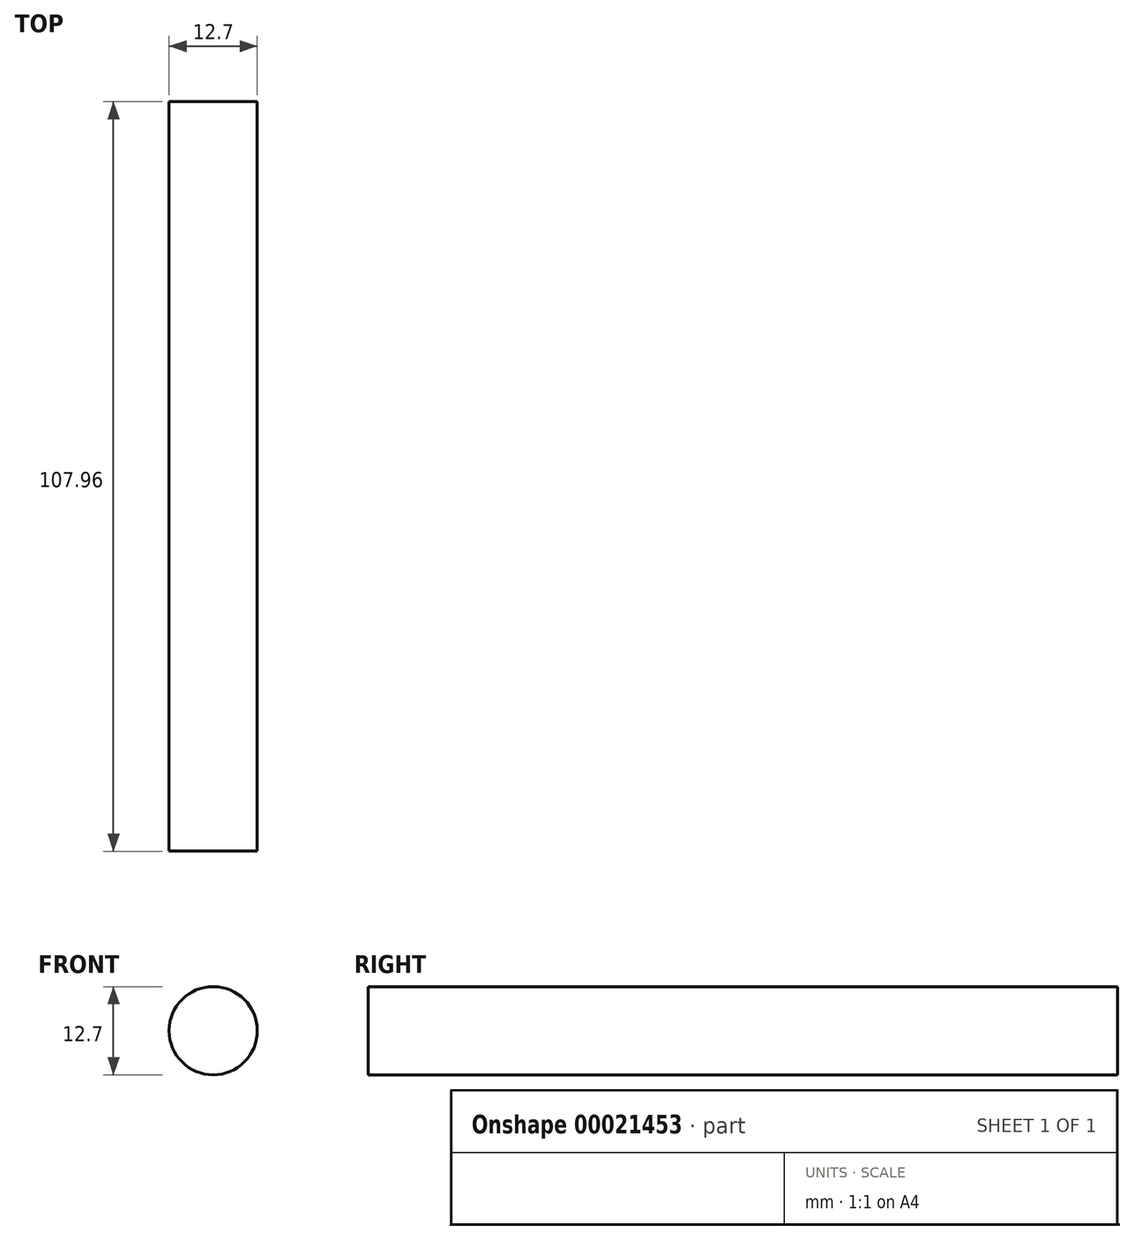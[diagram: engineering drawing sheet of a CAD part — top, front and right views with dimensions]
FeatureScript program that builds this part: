
annotation { "Feature Type Name" : "Feature", "Feature Type Description" : "" }
export const myFeature = defineFeature(function(context is Context, id is Id, definition is map)
    precondition{}
    {
        {
            var Q0;
            Q0=qCreatedBy(makeId("Front.planeOp"),FACE);
            var sketch = newSketch(context, id + "F0", { "sketchPlane" : qUnion([Q0])});
            skCircle(sketch, "E0", {"center": v(0, 0) * mm, "radius": 6.35 * mm});
            skSolve(sketch);
        }
        {
            var Q0;
            Q0=makeQuery(id+"F0.imprint","IMPRINT",FACE,{"disambiguationData":[TD([[makeQuery(id+"F0.imprint","IMPRINT",EDGE,{"derivedFrom":sQuery(id+"F0.wireOp",EDGE,"E0")}),1.0]])]});
            extrude(context, id + "F1", {"entities" : qUnion([Q0]), "endBound" : BoundingType.SYMMETRIC, "depth" : 107.95 * mm});
        }
    });
